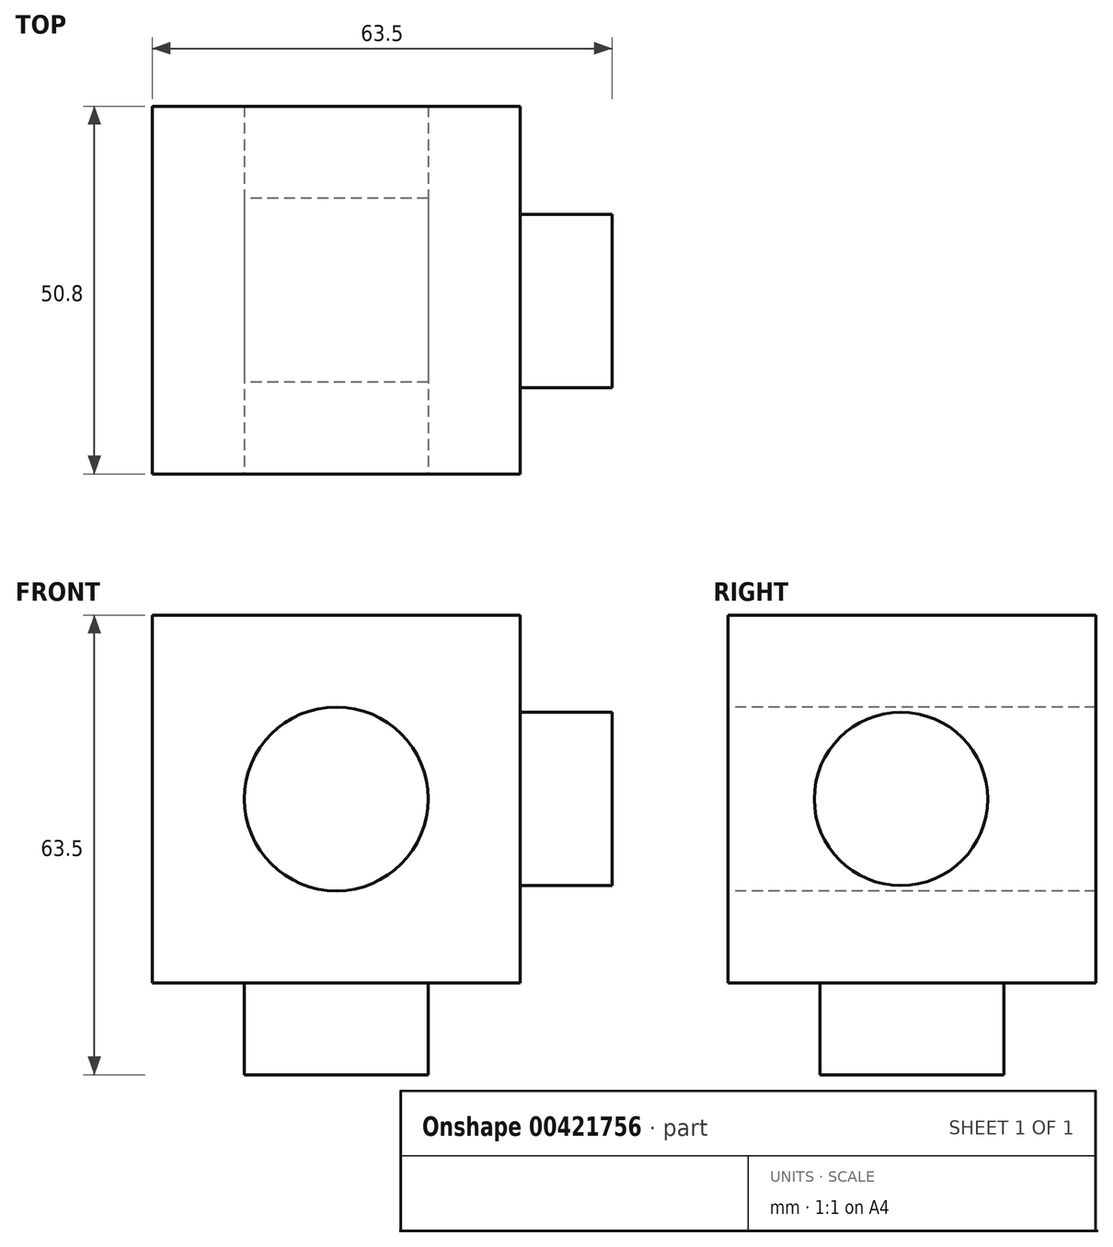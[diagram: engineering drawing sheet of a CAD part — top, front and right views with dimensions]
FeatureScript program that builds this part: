
annotation { "Feature Type Name" : "Feature", "Feature Type Description" : "" }
export const myFeature = defineFeature(function(context is Context, id is Id, definition is map)
    precondition{}
    {
        {
            var Q0;
            Q0=qCreatedBy(makeId("Front.planeOp"),FACE);
            var sketch = newSketch(context, id + "F0", { "sketchPlane" : qUnion([Q0])});
            skLineSegment(sketch, "E0.bottom", {"start": v(0, 0) * mm, "end": v(-50.8, 0) * mm});
            skLineSegment(sketch, "E0.top", {"start": v(0, 50.8) * mm, "end": v(-50.8, 50.8) * mm});
            skLineSegment(sketch, "E0.left", {"start": v(0, 0) * mm, "end": v(0, 50.8) * mm});
            skLineSegment(sketch, "E0.right", {"start": v(-50.8, 0) * mm, "end": v(-50.8, 50.8) * mm});
            skSolve(sketch);
        }
        {
            var Q0;
            Q0=makeQuery(id+"F0.imprint","IMPRINT",FACE,{"disambiguationData":[TD([[makeQuery(id+"F0.imprint","IMPRINT",EDGE,{"derivedFrom":sQuery(id+"F0.wireOp",EDGE,"E0.bottom")}),-1.0]])]});
            extrude(context, id + "F1", {"entities" : qUnion([Q0]), "depth" : 50.8 * mm});
        }
        {
            var Q0;
            Q0=makeQuery(id+"F1.opExtrude","CAP_FACE",FACE,{"disambiguationData":[OSD([sQuery(id+"F0.wireOp",EDGE,"E0.bottom"),sQuery(id+"F0.wireOp",EDGE,"E0.top"),sQuery(id+"F0.wireOp",EDGE,"E0.left"),sQuery(id+"F0.wireOp",EDGE,"E0.right")])],"isStart":false});
            var sketch = newSketch(context, id + "F2", { "sketchPlane" : qUnion([Q0])});
            skCircle(sketch, "E1", {"center": v(-25.4, 25.4) * mm, "radius": 12.7 * mm});
            skSolve(sketch);
        }
        {
            var Q0;
            Q0 = qSketchRegion(id + "F2", true);
            extrude(context, id + "F3", {"entities" : qUnion([Q0]), "operationType" : NewBodyOperationType.REMOVE, "oppositeDirection" : true, "depth" : 50.8 * mm});
        }
        {
            var Q0;
            Q0=makeQuery(id+"F1.opExtrude","SWEPT_FACE",FACE,{"disambiguationData":[OSD([sQuery(id+"F0.wireOp",EDGE,"E0.bottom")])]});
            var sketch = newSketch(context, id + "F4", { "sketchPlane" : qUnion([Q0])});
            skLineSegment(sketch, "E2.bottom", {"start": v(-12.7, 12.7) * mm, "end": v(-38.1, 12.7) * mm});
            skLineSegment(sketch, "E2.top", {"start": v(-12.7, 38.1) * mm, "end": v(-38.1, 38.1) * mm});
            skLineSegment(sketch, "E2.left", {"start": v(-12.7, 12.7) * mm, "end": v(-12.7, 38.1) * mm});
            skLineSegment(sketch, "E2.right", {"start": v(-38.1, 12.7) * mm, "end": v(-38.1, 38.1) * mm});
            skSolve(sketch);
        }
        {
            var Q0;
            Q0 = qSketchRegion(id + "F4", true);
            extrude(context, id + "F5", {"entities" : qUnion([Q0]), "operationType" : NewBodyOperationType.ADD, "depth" : 12.7 * mm});
        }
        {
            var Q0;
            Q0=makeQuery(id+"F1.opExtrude","SWEPT_FACE",FACE,{"disambiguationData":[OSD([sQuery(id+"F0.wireOp",EDGE,"E0.left")])]});
            var sketch = newSketch(context, id + "F6", { "sketchPlane" : qUnion([Q0])});
            skCircle(sketch, "E3", {"center": v(-26.91, 25.4) * mm, "radius": 11.97 * mm});
            skSolve(sketch);
        }
        {
            var Q0;
            Q0=makeQuery(id+"F6.imprint","IMPRINT",FACE,{"disambiguationData":[TD([[makeQuery(id+"F6.imprint","IMPRINT",EDGE,{"derivedFrom":sQuery(id+"F6.wireOp",EDGE,"E3")}),1.0]])]});
            extrude(context, id + "F7", {"entities" : qUnion([Q0]), "operationType" : NewBodyOperationType.ADD, "depth" : 12.7 * mm});
        }
    });
